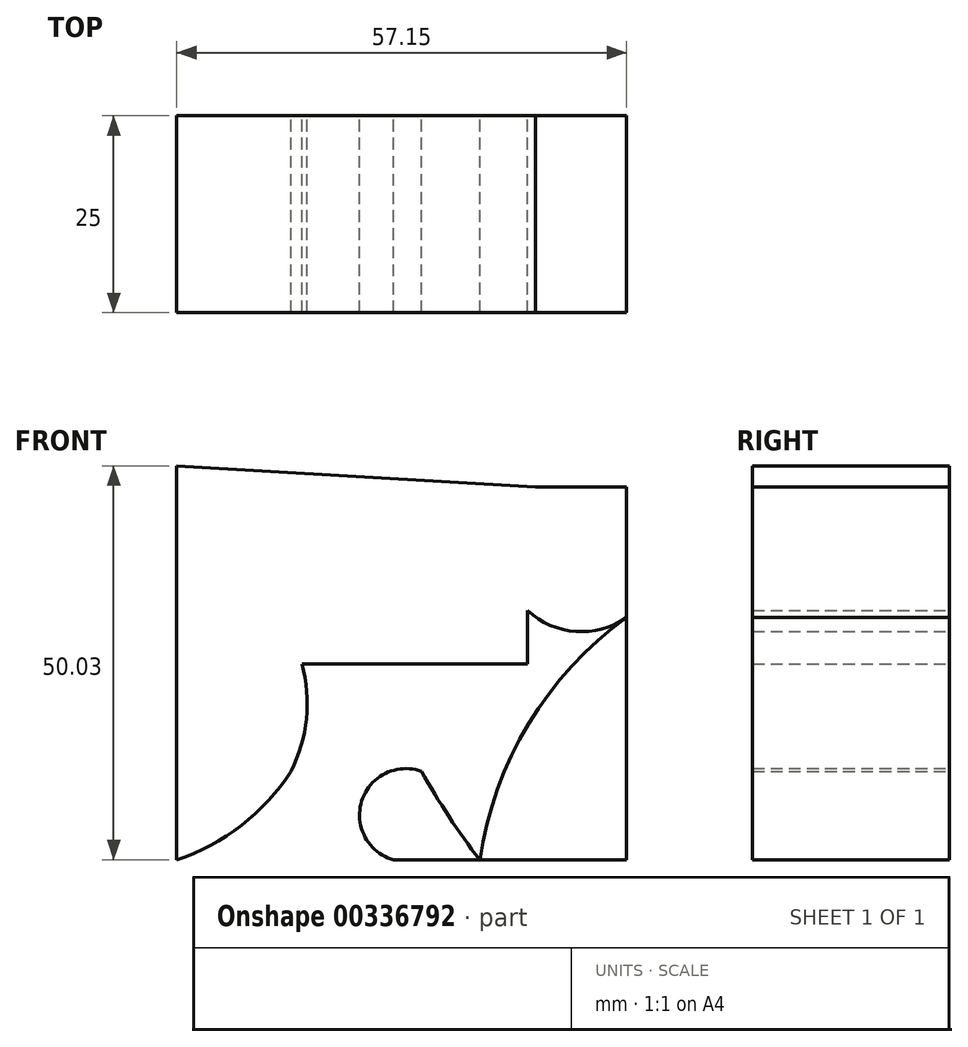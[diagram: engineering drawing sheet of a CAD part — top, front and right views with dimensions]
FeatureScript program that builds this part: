
annotation { "Feature Type Name" : "Feature", "Feature Type Description" : "" }
export const myFeature = defineFeature(function(context is Context, id is Id, definition is map)
    precondition{}
    {
        {
            var Q0;
            Q0=qCreatedBy(makeId("Front.planeOp"),FACE);
            var sketch = newSketch(context, id + "F0", { "sketchPlane" : qUnion([Q0])});
            skLineSegment(sketch, "E0", {"start": v(-38.49, 50.03) * mm, "end": v(-38.49, 0) * mm});
            skArc(sketch, "E1", {"start": v(-38.49, 0) * mm, "mid": v(-30.27, 4.38) * mm, "end": v(-23.98, 11.25) * mm});
            skArc(sketch, "E2", {"start": v(-23.98, 11.25) * mm, "mid": v(-22.6, 24.86) * mm, "end": v(-30.79, 35.82) * mm});
            skArc(sketch, "E3", {"start": v(-12, 48.49) * mm, "mid": v(-22.53, 43.83) * mm, "end": v(-30.79, 35.82) * mm});
            skArc(sketch, "E4", {"start": v(7.1, 47.37) * mm, "mid": v(4.6, 33.31) * mm, "end": v(18.66, 30.8) * mm});
            skArc(sketch, "E5", {"start": v(18.66, 30.8) * mm, "mid": v(6.21, 17.28) * mm, "end": v(0, 0) * mm});
            skArc(sketch, "E6", {"start": v(-7.4, 11.25) * mm, "mid": v(-3.92, 5.48) * mm, "end": v(0, 0) * mm});
            skArc(sketch, "E7", {"start": v(-7.4, 11.25) * mm, "mid": v(-15, 7.46) * mm, "end": v(-10.95, 0) * mm});
            skLineSegment(sketch, "E8", {"start": v(-38.49, 50.03) * mm, "end": v(7.1, 47.37) * mm});
            skLineSegment(sketch, "E9", {"start": v(7.1, 47.37) * mm, "end": v(18.66, 47.37) * mm});
            skLineSegment(sketch, "E10", {"start": v(18.66, 47.37) * mm, "end": v(18.66, 30.8) * mm});
            skLineSegment(sketch, "E11", {"start": v(18.66, 0) * mm, "end": v(-10.95, 0) * mm});
            skLineSegment(sketch, "E12", {"start": v(18.66, 30.8) * mm, "end": v(18.66, 0) * mm});
            skLineSegment(sketch, "E13", {"start": v(-22.6, 31.65) * mm, "end": v(6.06, 31.65) * mm});
            skLineSegment(sketch, "E14", {"start": v(6.06, 31.65) * mm, "end": v(6.06, 24.86) * mm});
            skPoint(sketch, "E14.endSnap0", {"position": v(-22.6, 24.86) * mm});
            skLineSegment(sketch, "E15", {"start": v(6.06, 24.86) * mm, "end": v(-22.6, 24.86) * mm});
            skLineSegment(sketch, "E16", {"start": v(-22.6, 24.86) * mm, "end": v(-22.6, 31.65) * mm});
            skSolve(sketch);
        }
        {
            var Q0;
            Q0 = qSketchRegion(id + "F0", true);
            extrude(context, id + "F1", {"entities" : qUnion([Q0]), "depth" : 25 * mm});
        }
        {
            var Q0;
            Q0 = qSketchRegion(id + "F0", true);
            extrude(context, id + "F2", {"entities" : qUnion([Q0]), "depth" : 25 * mm});
        }
    });
